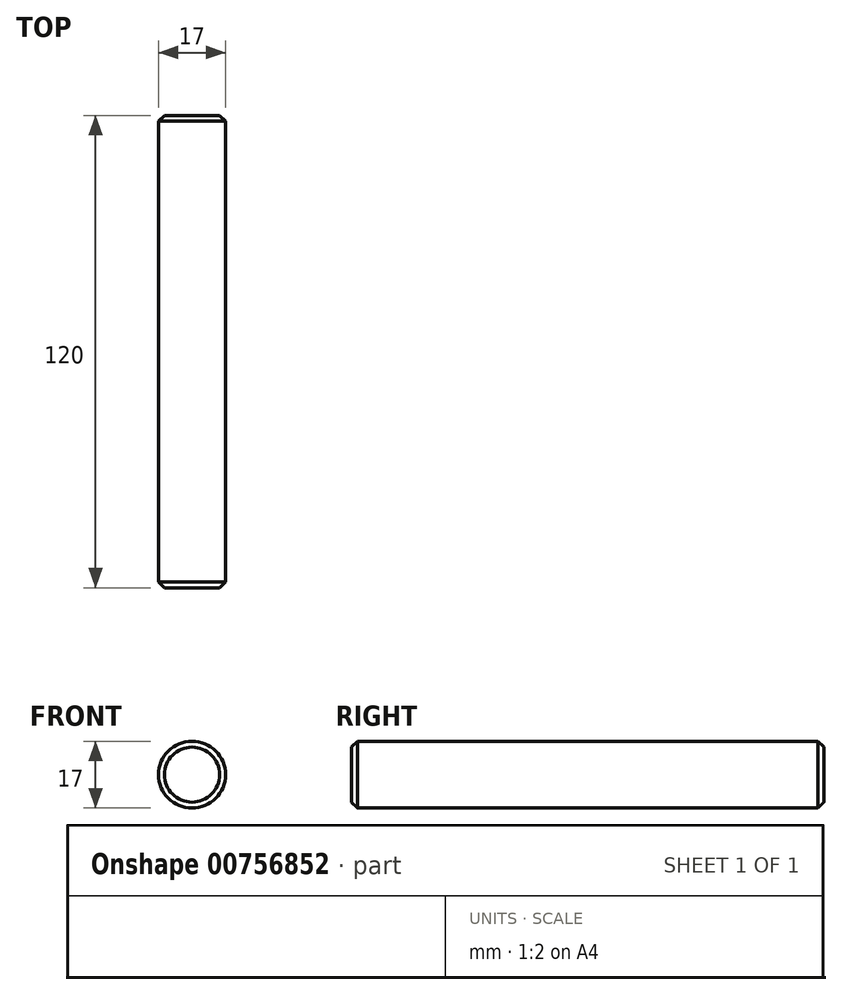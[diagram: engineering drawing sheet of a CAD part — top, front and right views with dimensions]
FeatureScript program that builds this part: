
annotation { "Feature Type Name" : "Feature", "Feature Type Description" : "" }
export const myFeature = defineFeature(function(context is Context, id is Id, definition is map)
    precondition{}
    {
        {
            var Q0;
            Q0=qCreatedBy(makeId("Front.planeOp"),FACE);
            var sketch = newSketch(context, id + "F0", { "sketchPlane" : qUnion([Q0])});
            skCircle(sketch, "E0", {"center": v(0, 0) * mm, "radius": 8.5 * mm});
            skSolve(sketch);
        }
        {
            var Q0;
            Q0=makeQuery(id+"F0.imprint","IMPRINT",FACE,{"disambiguationData":[TD([[makeQuery(id+"F0.imprint","IMPRINT",EDGE,{"derivedFrom":sQuery(id+"F0.wireOp",EDGE,"E0")}),1.0]])]});
            extrude(context, id + "F1", {"entities" : qUnion([Q0]), "depth" : 60 * mm, "offsetDistance" : 25 * mm, "hasSecondDirection" : true, "secondDirectionOppositeDirection" : true, "secondDirectionDepth" : 60 * mm});
        }
        {
            var Q0;
            Q0=makeQuery(id+"F1.opExtrude","CAP_EDGE",EDGE,{"disambiguationData":[OSD([sQuery(id+"F0.wireOp",EDGE,"E0")])],"isStart":false});
            var Q1;
            Q1=makeQuery(id+"F1.opExtrude","CAP_EDGE",EDGE,{"disambiguationData":[OSD([sQuery(id+"F0.wireOp",EDGE,"E0")])],"isStart":true});
            chamfer(context, id + "F2", {"entities" : qUnion([Q0, Q1]), "width" : 1.5 * mm, "tangentPropagation" : true});
        }
    });
